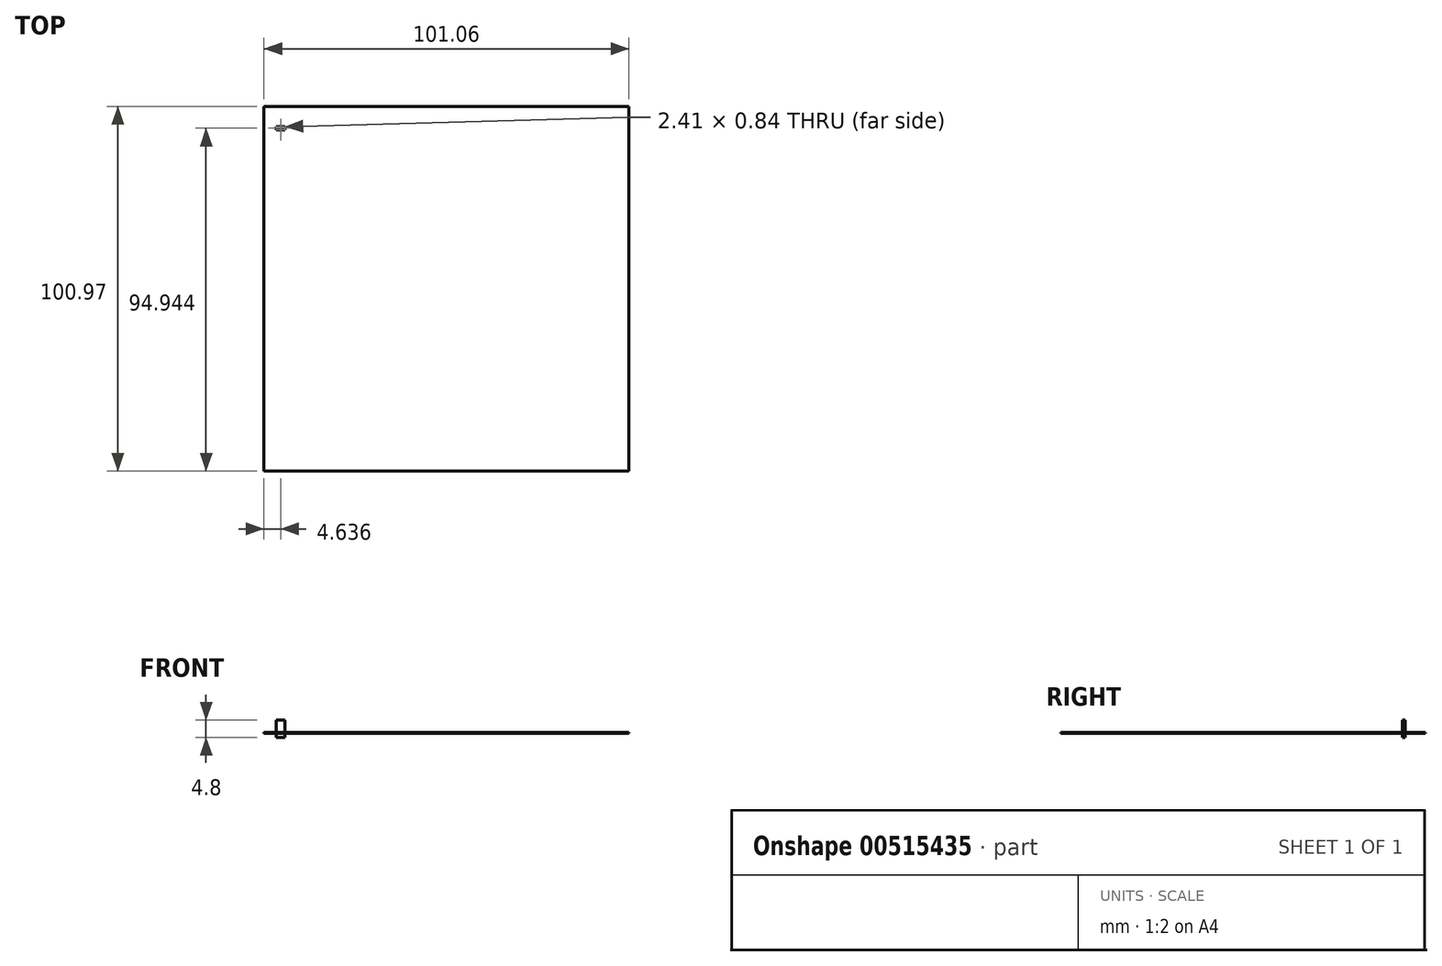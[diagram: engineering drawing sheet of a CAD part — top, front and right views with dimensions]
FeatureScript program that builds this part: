
annotation { "Feature Type Name" : "Feature", "Feature Type Description" : "" }
export const myFeature = defineFeature(function(context is Context, id is Id, definition is map)
    precondition{}
    {
        {
            var Q0;
            Q0=qCreatedBy(makeId("Top.planeOp"),FACE);
            var sketch = newSketch(context, id + "F0", { "sketchPlane" : qUnion([Q0])});
            skLineSegment(sketch, "E0.bottom", {"start": v(-105.27, 15.09) * mm, "end": v(-4.21, 15.09) * mm});
            skLineSegment(sketch, "E0.top", {"start": v(-105.27, -85.88) * mm, "end": v(-4.21, -85.88) * mm});
            skLineSegment(sketch, "E0.left", {"start": v(-105.27, 15.09) * mm, "end": v(-105.27, -85.88) * mm});
            skLineSegment(sketch, "E0.right", {"start": v(-4.21, 15.09) * mm, "end": v(-4.21, -85.88) * mm});
            skSolve(sketch);
        }
        {
            var Q0;
            Q0=makeQuery(id+"F0.imprint","IMPRINT",FACE,{"disambiguationData":[TD([[makeQuery(id+"F0.imprint","IMPRINT",EDGE,{"derivedFrom":sQuery(id+"F0.wireOp",EDGE,"E0.bottom")}),-1.0]])]});
            extrude(context, id + "F1", {"entities" : qUnion([Q0]), "depth" : .2 * mm, "offsetDistance" : 25 * mm});
        }
        {
            var Q0;
            Q0=qCreatedBy(makeId("Top.planeOp"),FACE);
            var sketch = newSketch(context, id + "F2", { "sketchPlane" : qUnion([Q0])});
            skLineSegment(sketch, "E1.bottom", {"start": v(-101.84, 9.49) * mm, "end": v(-99.43, 9.49) * mm});
            skLineSegment(sketch, "E1.top", {"start": v(-101.84, 8.64) * mm, "end": v(-99.43, 8.64) * mm});
            skLineSegment(sketch, "E1.left", {"start": v(-101.84, 9.49) * mm, "end": v(-101.84, 8.64) * mm});
            skLineSegment(sketch, "E1.right", {"start": v(-99.43, 9.49) * mm, "end": v(-99.43, 8.64) * mm});
            skSolve(sketch);
        }
        {
            var Q0;
            Q0 = qSketchRegion(id + "F2", true);
            extrude(context, id + "F3", {"entities" : qUnion([Q0]), "operationType" : NewBodyOperationType.ADD, "depth" : 3.6 * mm, "offsetDistance" : 25 * mm, "hasSecondDirection" : true, "secondDirectionOppositeDirection" : true, "secondDirectionDepth" : 1.2 * mm});
        }
    });
